# Revit family: RN 92017 Optifitt-Serra-Raccordo
name_source: partatom
category: Rohrformteile
units: mm (PartAtom-declared; Revit-internal decimal feet)

## family parameters
Arbeitsebenenbasiert = Nein
Beim Laden mit Abzugskörper schneiden = Nein
Bemaßung runder Anschluss = Durchmesser verwenden
Gemeinsam genutzt = Nein
Immer vertikal = Ja
Teiletyp = Verbindung

## types (2) — shared parameters
1.010.00.2 Blattnummer der Richtlinie = 29
1.010.00.3 Ausgabedatum (Monat) der Richtlinie = 201308
1.010.00.4 Herstellername = R. Nussbaum AG
1.010.00.5 Revisionsdatum der Datei = 20190521
1.010.00.6 Webadresse des Herstellers = http://www.nussbaum.ch
1.100.00.4 Produktbezeichnung = Versorgung
1.110.00.2 Index = 3
1.110.00.4 Produktbezeichnung = Optifitt-Serra
1.960/3L.00.8 Link (URL) = https://www.nussbaum.ch
29.700.00.4 Produktname = Optifitt-Serra-Anschlussverschraubung, absperrbar mit Kugelhahn
29.700.00.5 Produktkennung = 2
29.700.00.6 Querschnittsform = 1
29.700.00.7 Nennweitensystem = DN
29.700.00.8 Nenndrucksystem = PN
29.710.02.4 Nenndruck = 10
29.710.02.5 max. zul. Überdruck [hPa] = 1000
29.710.02.7 max. zul. Dauer-Betriebsdruck [hPa] = 1000
29.710.02.9 max. zul. Dauer-Betriebstemperatur [°C] = 90
Connector Visibility = Nein
EnclosingSpace Visibility = Nein
Hersteller = R. Nussbaum AG
URL = https://www.nussbaum.ch

## per-type parameters (varying)
| type | 1.800.00.3 TGA-Nummer | 1.800.00.4 Kommentarfeld | 1.810.00.3 Hersteller-Bestellnummer | 1.810.00.4 DATANORM-Nummer | 1.810.00.5 StLB-Nummer | 1.810.00.6 GTIN-Nummer | 29.710.02.10 Formstück-Gewicht [kg] | 29.710.02.3 Benennung | CONNECTOR0_DIAMETER_dX_0r | CONNECTOR0_dX_01 | CONNECTOR0_ref_dX | CONNECTOR1_DIAMETER_dX_0r | CONNECTOR1_dX_00 | CONNECTOR1_dX_01 | CONNECTOR1_ref_dX | Modell | R. Nussbaum AG 92017.04 de Visibility | R. Nussbaum AG 92017.05 de Visibility | Typenkommentare |
| DN=20 | 01900300000000000000000000000000000000000000000040000000000000000002 | 92017.05, Optifitt-Serra-Anschlussverschraubung, absperrbar mit Kugelhahn, DN=20, L=77 | 92017.05 | 92017.05 | 671.714 | 7612945681874 | 0.24 | Optifitt-Serra-Anschlussverschraubung, absperrbar mit Kugelhahn, DN=20, L=77 | 20 mm | 15 mm  [stored 0.0492126 ft] | 15 mm  [stored 0.0492126 ft] | 25 mm  [stored 0.082021 ft] | 60 mm | 77 mm | 60 mm | 92017.05 | Nein | Ja | Optifitt-Serra-Raccordo  DN=20 |
| DN=15 | 01900300000000000000000000000000000000000000000040000000000000000001 | 92017.04, Optifitt-Serra-Anschlussverschraubung, absperrbar mit Kugelhahn, DN=15, L=74 | 92017.04 | 92017.04 | 671.713 | 7612945681867 | 0.196 | Optifitt-Serra-Anschlussverschraubung, absperrbar mit Kugelhahn, DN=15, L=74 | 15 mm  [stored 0.0492126 ft] | 13 mm | 13 mm | 20 mm | 59 mm | 74 mm | 59 mm | 92017.04 | Ja | Nein | Optifitt-Serra-Raccordo  DN=15 |

note: [stored X ft] marks values corroborated as IEEE doubles in the binary element streams (Revit-internal decimal feet)

## geometry (parser evidence)
native form markers: Sweep x2
no freeform markers — native parametric forms only
